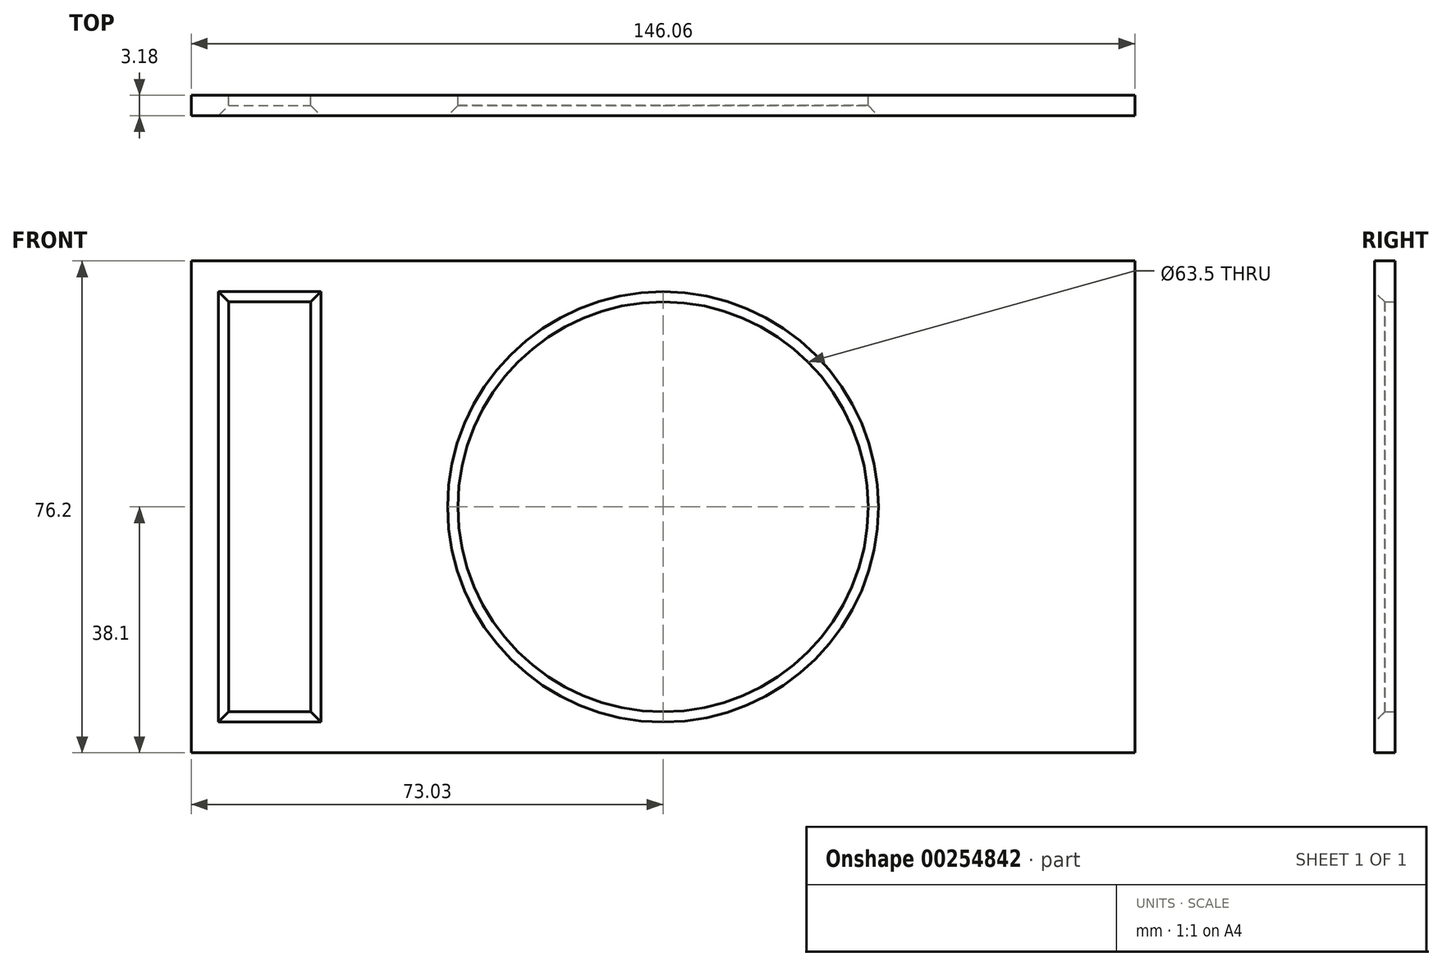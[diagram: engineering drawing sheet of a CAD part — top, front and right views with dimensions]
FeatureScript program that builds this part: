
annotation { "Feature Type Name" : "Feature", "Feature Type Description" : "" }
export const myFeature = defineFeature(function(context is Context, id is Id, definition is map)
    precondition{}
    {
        {
            var Q0;
            Q0=qCreatedBy(makeId("Front.planeOp"),FACE);
            var sketch = newSketch(context, id + "F0", { "sketchPlane" : qUnion([Q0])});
            skLineSegment(sketch, "E0.bottom", {"start": v(-73.03, -38.1) * mm, "end": v(73.03, -38.1) * mm});
            skLineSegment(sketch, "E0.top", {"start": v(-73.03, 38.1) * mm, "end": v(73.02, 38.1) * mm});
            skLineSegment(sketch, "E0.left", {"start": v(-73.02, -38.1) * mm, "end": v(-73.03, 38.1) * mm});
            skLineSegment(sketch, "E0.right", {"start": v(73.03, -38.1) * mm, "end": v(73.02, 38.1) * mm});
            skPoint(sketch, "E0.middle", {"position": v(0, 0) * mm});
            skLineSegment(sketch, "E1.bottom", {"start": v(-67.21, -31.75) * mm, "end": v(-54.51, -31.75) * mm});
            skLineSegment(sketch, "E1.top", {"start": v(-67.21, 31.75) * mm, "end": v(-54.51, 31.75) * mm});
            skLineSegment(sketch, "E1.left", {"start": v(-67.21, -31.75) * mm, "end": v(-67.21, 31.75) * mm});
            skLineSegment(sketch, "E1.right", {"start": v(-54.51, -31.75) * mm, "end": v(-54.51, 31.75) * mm});
            skPoint(sketch, "E1.middle", {"position": v(-60.86, 0) * mm});
            skCircle(sketch, "E2", {"center": v(0, 0) * mm, "radius": 31.75 * mm});
            skSolve(sketch);
        }
        {
            var Q0;
            Q0=makeQuery(id+"F0.imprint","IMPRINT",FACE,{"disambiguationData":[TD([[makeQuery(id+"F0.imprint","IMPRINT",EDGE,{"derivedFrom":sQuery(id+"F0.wireOp",EDGE,"E0.bottom")}),1.0]])]});
            extrude(context, id + "F1", {"entities" : qUnion([Q0]), "endBound" : BoundingType.SYMMETRIC, "depth" : 3.17 * mm});
        }
        {
            var Q0;
            Q0=makeQuery(id+"F1.opExtrude","CAP_EDGE",EDGE,{"disambiguationData":[OSD([sQuery(id+"F0.wireOp",EDGE,"E1.right")])],"isStart":false});
            var Q1;
            Q1=makeQuery(id+"F1.opExtrude","CAP_EDGE",EDGE,{"disambiguationData":[OSD([sQuery(id+"F0.wireOp",EDGE,"E1.bottom")])],"isStart":false});
            var Q2;
            Q2=makeQuery(id+"F1.opExtrude","CAP_EDGE",EDGE,{"disambiguationData":[OSD([sQuery(id+"F0.wireOp",EDGE,"E1.left")])],"isStart":false});
            var Q3;
            Q3=makeQuery(id+"F1.opExtrude","CAP_EDGE",EDGE,{"disambiguationData":[OSD([sQuery(id+"F0.wireOp",EDGE,"E1.top")])],"isStart":false});
            chamfer(context, id + "F2", {"entities" : qUnion([Q0, Q1, Q2, Q3]), "width" : 1.59 * mm, "tangentPropagation" : true});
        }
        {
            var Q0;
            Q0=makeQuery(id+"F1.opExtrude","CAP_EDGE",EDGE,{"disambiguationData":[OSD([sQuery(id+"F0.wireOp",EDGE,"E2")])],"isStart":false});
            chamfer(context, id + "F3", {"entities" : qUnion([Q0]), "width" : 1.59 * mm, "tangentPropagation" : true});
        }
    });
